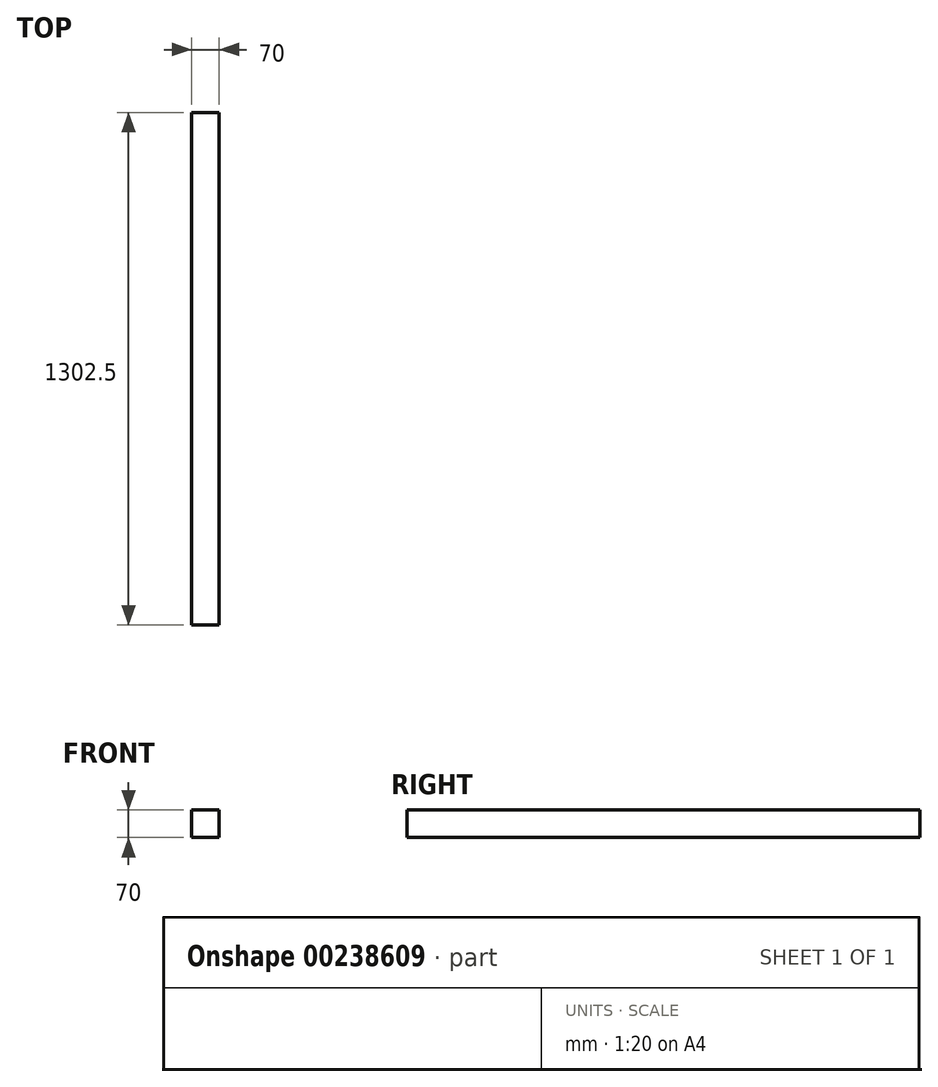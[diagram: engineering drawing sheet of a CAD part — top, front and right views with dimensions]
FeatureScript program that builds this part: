
annotation { "Feature Type Name" : "Feature", "Feature Type Description" : "" }
export const myFeature = defineFeature(function(context is Context, id is Id, definition is map)
    precondition{}
    {
        {
            var Q0;
            Q0=qCreatedBy(makeId("Front.planeOp"),FACE);
            var sketch = newSketch(context, id + "F0", { "sketchPlane" : qUnion([Q0])});
            skLineSegment(sketch, "E0.bottom", {"start": v(35, -35) * mm, "end": v(-35, -35) * mm});
            skLineSegment(sketch, "E0.top", {"start": v(35, 35) * mm, "end": v(-35, 35) * mm});
            skLineSegment(sketch, "E0.left", {"start": v(35, -35) * mm, "end": v(35, 35) * mm});
            skLineSegment(sketch, "E0.right", {"start": v(-35, -35) * mm, "end": v(-35, 35) * mm});
            skPoint(sketch, "E0.middle", {"position": v(0, 0) * mm});
            skSolve(sketch);
        }
        {
            var Q0;
            Q0=makeQuery(id+"F0.imprint","IMPRINT",FACE,{"disambiguationData":[TD([[makeQuery(id+"F0.imprint","IMPRINT",EDGE,{"derivedFrom":sQuery(id+"F0.wireOp",EDGE,"E0.bottom")}),-1.0]])]});
            extrude(context, id + "F1", {"entities" : qUnion([Q0]), "depth" : 1302.5 * mm});
        }
    });
